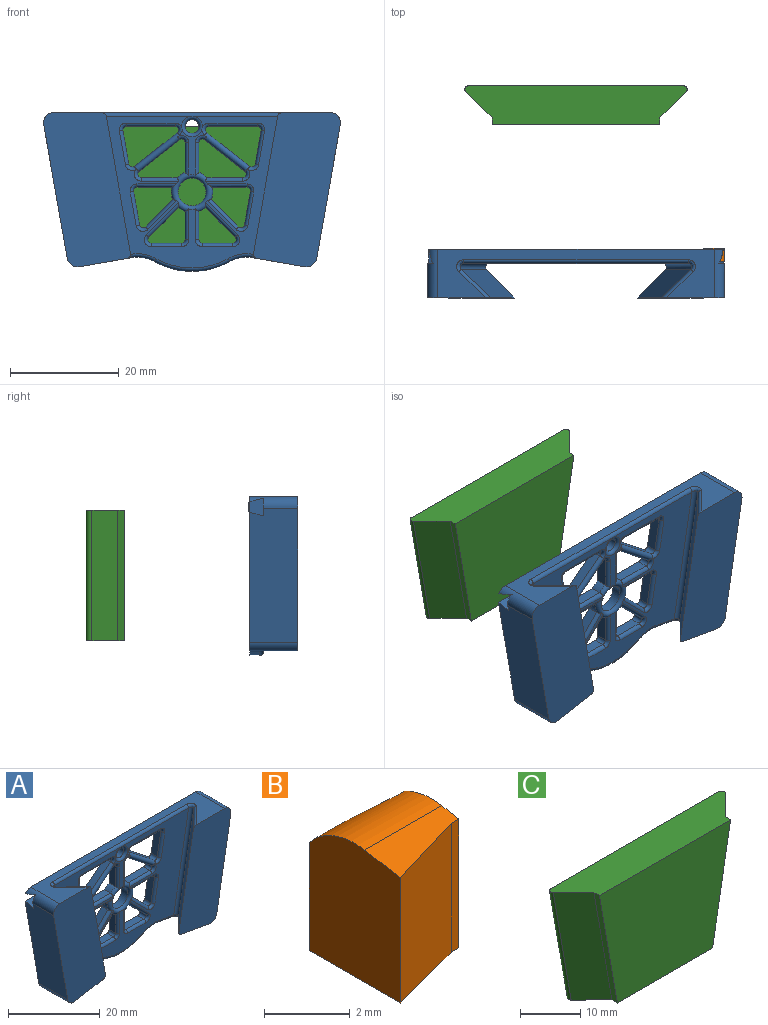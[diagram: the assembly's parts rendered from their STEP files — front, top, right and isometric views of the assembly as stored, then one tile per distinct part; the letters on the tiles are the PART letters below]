
ASSEMBLY  parts=3 mates=2
PART A: 135 faces, bbox 54.6x9.3x30.4 mm
  f0: cylinder r=1.91mm len=8.89mm, axis (0,1,0), area 25.1mm2, adj f1,f4,f5,f15,f131,f132
  f1: plane 24.58x8.89mm, normal (-0.98,0,-0.17), area 219.4mm2, adj f0,f4,f6,f15,f132,f133
  f2: plane 8.44x5.38mm, normal (0,-1,0), area 10.7mm2, adj f105,f107,f108,f112,f113,f118,f119,f124
  f3: plane 41.31x27.94mm, normal (0,-1,0), area 479.4mm2, adj f69,f70,f71,f73,f76,f77,f81,f82
  f4: plane 54.33x29.21mm, normal (0,1,0), area 1066.4mm2, adj f0,f1,f5,f6,f7,f8,f9,f10
  f5: plane 50.8x8.89mm, normal (0,0,1), area 173.2mm2, adj f0,f4,f14,f15,f16,f78,f80,f82
  f6: cylinder r=1.91mm len=8.89mm, axis (0,1,0), area 26.6mm2, adj f1,f4,f7,f15
  f7: plane 9.56x8.89mm, normal (0.17,0,-0.98), area 57.7mm2, adj f4,f6,f8,f15,f71,f72,f74
  f8: cylinder r=6.35mm len=4.21mm, axis (0,1,0), area 8.3mm2, adj f4,f7,f9,f69
  f9: cylinder r=14.2mm len=13.92mm, axis (0,1,0), area 27.7mm2, adj f4,f8,f10,f70
  f10: cylinder r=6.35mm len=4.21mm, axis (0,1,0), area 8.3mm2, adj f4,f9,f11,f73
  f11: plane 9.56x8.89mm, normal (-0.17,0,-0.98), area 57.7mm2, adj f4,f10,f12,f16,f75,f76,f79
  f12: cylinder r=1.91mm len=8.89mm, axis (0,1,0), area 26.6mm2, adj f4,f11,f13,f16
  f13: plane 24.58x8.89mm, normal (0.98,0,-0.17), area 219.4mm2, adj f4,f12,f14,f16,f127,f128
  f14: cylinder r=1.91mm len=8.89mm, axis (0,1,0), area 25.1mm2, adj f4,f5,f13,f16,f127,f129
  f15: plane 28.39x16.03mm, normal (0,-1,0), area 324.3mm2, adj f0,f1,f5,f6,f7,f17,f72,f78
  f16: plane 28.39x16.03mm, normal (0,-1,0), area 324.3mm2, adj f5,f11,f12,f13,f14,f18,f75,f84
  f17: plane 26.4x9.84mm, normal (0.7,0.71,0.12), area 196.2mm2, adj f15,f72,f77,f78
  f18: plane 26.4x9.84mm, normal (-0.7,0.71,0.12), area 196.2mm2, adj f16,f75,f81,f84
  f19: plane 5.2x1.91mm, normal (-1,0,0), area 9.9mm2, adj f4,f20,f22,f101
  f20: cylinder r=3.81mm len=1.91mm, axis (0,-1,0), area 2.7mm2, adj f4,f19,f21,f105
  f21: plane 5.47x5.47mm, normal (0.71,0,-0.71), area 14.7mm2, adj f4,f20,f23,f102
  f22: cylinder r=0.64mm len=1.91mm, axis (0,-1,0), area 1.9mm2, adj f4,f19,f24,f93
  f23: cylinder r=0.64mm len=1.91mm, axis (0,-1,0), area 2.9mm2, adj f4,f21,f24,f94
  f24: plane 5.62x1.91mm, normal (0,0,1), area 10.7mm2, adj f4,f22,f23,f87
  f25: cylinder r=1.27mm len=2.54mm, axis (0,-1,0), area 15.2mm2, adj f4,f126
  f26: cylinder r=2.54mm len=5.08mm, axis (0,-1,0), area 30.4mm2, adj f4,f105
  f27: plane 7.45x5.85mm, normal (-0.62,0,-0.79), area 18mm2, adj f4,f28,f30,f118
  f28: cylinder r=0.64mm len=1.91mm, axis (0,-1,0), area 2.7mm2, adj f4,f27,f29,f112
  f29: plane 5.55x1.91mm, normal (1,0,0), area 10.6mm2, adj f4,f28,f31,f107
  f30: cylinder r=0.64mm len=1.91mm, axis (0,-1,0), area 3mm2, adj f4,f27,f32,f111
  f31: cylinder r=3.81mm len=1.91mm, axis (0,-1,0), area 3.3mm2, adj f4,f29,f32,f105
  f32: plane 6.62x1.91mm, normal (0,0,1), area 12.6mm2, adj f4,f30,f31,f106
  f33: cylinder r=0.64mm len=1.91mm, axis (0,-1,0), area 1.9mm2, adj f4,f34,f36,f92
  f34: plane 5.62x1.91mm, normal (0,0,1), area 10.7mm2, adj f4,f33,f35,f86
  f35: cylinder r=0.64mm len=1.91mm, axis (0,-1,0), area 2.9mm2, adj f4,f34,f37,f91
  f36: plane 5.2x1.91mm, normal (1,0,0), area 9.9mm2, adj f4,f33,f38,f100
  f37: plane 5.47x5.47mm, normal (-0.71,0,-0.71), area 14.7mm2, adj f4,f35,f38,f99
  f38: cylinder r=3.81mm len=1.91mm, axis (0,-1,0), area 2.7mm2, adj f4,f36,f37,f105
  f39: plane 5.03x5.03mm, normal (0.71,0,0.71), area 13.5mm2, adj f4,f40,f42,f98
  f40: cylinder r=0.64mm len=1.91mm, axis (0,-1,0), area 2.6mm2, adj f4,f39,f41,f90
  f41: plane 6.22x1.91mm, normal (-0.98,0,0.17), area 12mm2, adj f4,f40,f43,f85
  f42: cylinder r=3.81mm len=2.27mm, axis (0,-1,0), area 4.4mm2, adj f4,f39,f44,f105
  f43: cylinder r=0.64mm len=1.91mm, axis (0,-1,0), area 2.1mm2, adj f4,f41,f44,f89
  f44: plane 6.41x1.91mm, normal (0,0,-1), area 12.2mm2, adj f4,f42,f43,f97
  f45: cylinder r=0.64mm len=1.91mm, axis (0,-1,0), area 3mm2, adj f4,f46,f48,f125
  f46: plane 8.99x1.91mm, normal (0,0,-1), area 17.1mm2, adj f4,f45,f47,f123
  f47: cylinder r=0.64mm len=1.91mm, axis (0,-1,0), area 2.1mm2, adj f4,f46,f49,f121
  f48: plane 7.9x6.21mm, normal (-0.62,0,0.79), area 19.1mm2, adj f4,f45,f50,f119
  f49: plane 6.21x1.91mm, normal (0.98,0,0.17), area 12mm2, adj f4,f47,f50,f115
  f50: cylinder r=0.64mm len=1.91mm, axis (0,-1,0), area 2.5mm2, adj f4,f48,f49,f120
  f51: plane 6.41x1.91mm, normal (0,0,-1), area 12.2mm2, adj f4,f52,f54,f104
  f52: cylinder r=0.64mm len=1.91mm, axis (0,-1,0), area 2.1mm2, adj f4,f51,f53,f96
  f53: plane 6.22x1.91mm, normal (0.98,0,0.17), area 12mm2, adj f4,f52,f55,f88
  f54: cylinder r=3.81mm len=2.27mm, axis (0,-1,0), area 4.4mm2, adj f4,f51,f56,f105
  f55: cylinder r=0.64mm len=1.91mm, axis (0,-1,0), area 2.6mm2, adj f4,f53,f56,f95
  f56: plane 5.03x5.03mm, normal (-0.71,0,0.71), area 13.5mm2, adj f4,f54,f55,f103
  f57: cylinder r=3.81mm len=1.91mm, axis (0,-1,0), area 3.3mm2, adj f4,f58,f62,f105
  f58: plane 5.55x1.91mm, normal (-1,0,0), area 10.6mm2, adj f4,f57,f59,f108
  f59: cylinder r=0.64mm len=1.91mm, axis (0,-1,0), area 2.7mm2, adj f4,f58,f60,f113
  f60: plane 7.45x5.85mm, normal (0.62,0,-0.79), area 18mm2, adj f4,f59,f61,f119
  f61: cylinder r=0.64mm len=1.91mm, axis (0,-1,0), area 3mm2, adj f4,f60,f62,f114
  f62: plane 6.62x1.91mm, normal (0,0,1), area 12.6mm2, adj f4,f57,f61,f109
  f63: plane 8.99x1.91mm, normal (0,0,-1), area 17.1mm2, adj f4,f64,f68,f122
  f64: cylinder r=0.64mm len=1.91mm, axis (0,-1,0), area 3mm2, adj f4,f63,f65,f124
  f65: plane 7.9x6.21mm, normal (0.62,0,0.79), area 19.1mm2, adj f4,f64,f66,f118
  f66: cylinder r=0.64mm len=1.91mm, axis (0,-1,0), area 2.5mm2, adj f4,f65,f67,f117
  f67: plane 6.21x1.91mm, normal (-0.98,0,0.17), area 12mm2, adj f4,f66,f68,f110
  f68: cylinder r=0.64mm len=1.91mm, axis (0,-1,0), area 2.1mm2, adj f4,f63,f67,f116
  f69: torus R=6.99mm, axis (0,-1,0), area 4.5mm2, adj f3,f8,f70,f71
  f70: torus R=13.56mm, axis (0,-1,0), area 14.3mm2, adj f3,f9,f69,f73
  f71: cylinder r=0.64mm len=4.85mm, axis (0.98,0,0.17), area 4.8mm2, adj f3,f7,f69,f74
  f72: cylinder r=0.64mm len=5.72mm, axis (0.7,-0.71,0.12), area 7.2mm2, adj f7,f15,f17,f74
  f73: torus R=6.99mm, axis (0,-1,0), area 4.5mm2, adj f3,f10,f70,f76
  f74: torus R=1.27mm, axis (0.17,0,-0.98), area 2mm2, adj f7,f71,f72,f77
  f75: cylinder r=0.64mm len=5.72mm, axis (-0.7,-0.71,0.12), area 7.2mm2, adj f11,f16,f18,f79
  f76: cylinder r=0.64mm len=4.85mm, axis (0.98,0,-0.17), area 4.8mm2, adj f3,f11,f73,f79
  f77: cylinder r=0.64mm len=26.58mm, axis (0.17,0,-0.98), area 40.1mm2, adj f3,f17,f74,f80
  f78: cylinder r=0.64mm len=5.79mm, axis (0.71,-0.7,0), area 6.7mm2, adj f5,f15,f17,f80
  f79: torus R=1.27mm, axis (0.17,0,0.98), area 2mm2, adj f11,f75,f76,f81
  f80: bspline ~2.31x1.51mm, area 1.9mm2, adj f5,f77,f78,f82
  f81: cylinder r=0.64mm len=26.58mm, axis (0.17,0,0.98), area 40.1mm2, adj f3,f18,f79,f83
  f82: cylinder r=0.64mm len=41.31mm, axis (1,0,0), area 41.2mm2, adj f3,f5,f80,f83
  f83: bspline ~2.18x1.3mm, area 1.9mm2, adj f5,f81,f82,f84
  f84: cylinder r=0.64mm len=5.79mm, axis (0.71,0.7,0), area 6.7mm2, adj f5,f16,f18,f83
  f85: cylinder r=0.64mm len=6.33mm, axis (-0.17,0,-0.98), area 6.3mm2, adj f3,f41,f89,f90
  f86: cylinder r=0.64mm len=5.62mm, axis (-1,0,0), area 5.6mm2, adj f3,f34,f91,f92
  f87: cylinder r=0.64mm len=5.62mm, axis (-1,0,0), area 5.6mm2, adj f3,f24,f93,f94
  f88: cylinder r=0.64mm len=6.33mm, axis (-0.17,0,0.98), area 6.3mm2, adj f3,f53,f95,f96
  f89: torus R=1.27mm, axis (0,-1,0), area 1.5mm2, adj f3,f43,f85,f97
  f90: torus R=1.27mm, axis (0,-1,0), area 1.9mm2, adj f3,f40,f85,f98
  f91: torus R=1.27mm, axis (0,-1,0), area 2mm2, adj f3,f35,f86,f99
  f92: torus R=1.27mm, axis (0,-1,0), area 1.4mm2, adj f3,f33,f86,f100
  f93: torus R=1.27mm, axis (0,-1,0), area 1.4mm2, adj f3,f22,f87,f101
  f94: torus R=1.27mm, axis (0,-1,0), area 2mm2, adj f3,f23,f87,f102
  f95: torus R=1.27mm, axis (0,-1,0), area 1.9mm2, adj f3,f55,f88,f103
  f96: torus R=1.27mm, axis (0,-1,0), area 1.5mm2, adj f3,f52,f88,f104
  f97: cylinder r=0.64mm len=7.32mm, axis (1,0,0), area 6.7mm2, adj f3,f44,f89,f105
  f98: cylinder r=0.64mm len=5.79mm, axis (-0.71,0,0.71), area 7.3mm2, adj f3,f39,f90,f105
  f99: cylinder r=0.64mm len=6.38mm, axis (0.71,0,-0.71), area 7.9mm2, adj f3,f37,f91,f105
  f100: cylinder r=0.64mm len=5.68mm, axis (0,0,1), area 5.4mm2, adj f3,f36,f92,f105
  f101: cylinder r=0.64mm len=5.68mm, axis (0,0,-1), area 5.4mm2, adj f3,f19,f93,f105
  f102: cylinder r=0.64mm len=6.38mm, axis (0.71,0,0.71), area 7.9mm2, adj f3,f21,f94,f105
  f103: cylinder r=0.64mm len=5.79mm, axis (-0.71,0,-0.71), area 7.3mm2, adj f3,f56,f95,f105
  f104: cylinder r=0.64mm len=7.32mm, axis (1,0,0), area 6.7mm2, adj f3,f51,f96,f105
  f105: torus R=3.17mm, axis (0,-1,0), area 29.8mm2, adj f2,f3,f20,f26,f31,f38,f42,f54
  f106: cylinder r=0.64mm len=6.9mm, axis (-1,0,0), area 6.7mm2, adj f3,f32,f105,f111
  f107: cylinder r=0.64mm len=6.03mm, axis (0,0,1), area 5.7mm2, adj f2,f29,f105,f112
  f108: cylinder r=0.64mm len=6.03mm, axis (0,0,-1), area 5.7mm2, adj f2,f58,f105,f113
  f109: cylinder r=0.64mm len=6.9mm, axis (-1,0,0), area 6.7mm2, adj f3,f62,f105,f114
  f110: cylinder r=0.64mm len=6.32mm, axis (-0.17,0,-0.98), area 6.3mm2, adj f3,f67,f116,f117
  f111: torus R=1.27mm, axis (0,-1,0), area 2.1mm2, adj f3,f30,f106,f118
  f112: torus R=1.27mm, axis (0,-1,0), area 1.9mm2, adj f2,f28,f107,f118
  f113: torus R=1.27mm, axis (0,-1,0), area 1.9mm2, adj f2,f59,f108,f119
  f114: torus R=1.27mm, axis (0,-1,0), area 2.1mm2, adj f3,f61,f109,f119
  f115: cylinder r=0.64mm len=6.32mm, axis (-0.17,0,0.98), area 6.3mm2, adj f3,f49,f120,f121
  f116: torus R=1.27mm, axis (0,-1,0), area 1.5mm2, adj f3,f68,f110,f122
  f117: torus R=1.27mm, axis (0,-1,0), area 1.8mm2, adj f3,f66,f110,f118
  f118: cylinder r=0.64mm len=8.68mm, axis (0.79,0,-0.62), area 19.5mm2, adj f2,f3,f27,f65,f111,f112,f117,f124
  f119: cylinder r=0.64mm len=8.68mm, axis (0.79,0,0.62), area 19.5mm2, adj f2,f3,f48,f60,f113,f114,f120,f125
  f120: torus R=1.27mm, axis (0,-1,0), area 1.8mm2, adj f3,f50,f115,f119
  f121: torus R=1.27mm, axis (0,-1,0), area 1.5mm2, adj f3,f47,f115,f123
  f122: cylinder r=0.64mm len=8.99mm, axis (1,0,0), area 9mm2, adj f3,f63,f116,f124
  f123: cylinder r=0.64mm len=8.99mm, axis (1,0,0), area 9mm2, adj f3,f46,f121,f125
  f124: torus R=1.27mm, axis (0,-1,0), area 2.1mm2, adj f2,f3,f64,f118,f122,f126
  f125: torus R=1.27mm, axis (0,-1,0), area 2.1mm2, adj f2,f3,f45,f119,f123,f126
  f126: torus R=1.91mm, axis (0,-1,0), area 9.4mm2, adj f2,f3,f25,f124,f125
  f127: plane 3.81x3.27mm, normal (0,1,0), area 11.8mm2, adj f13,f14,f128,f129,f130
  f128: plane 3.67x2.54mm, normal (0,-0.26,0.97), area 9.5mm2, adj f4,f13,f127,f130
  f129: plane 3.55x2.54mm, normal (0,-0.26,-0.97), area 8.6mm2, adj f4,f14,f127,f130
  f130: plane 3.27x2.54mm, normal (1,0,0), area 6.6mm2, adj f4,f127,f128,f129
  f131: plane 3.55x2.54mm, normal (0,-0.26,-0.97), area 8.6mm2, adj f0,f4,f132,f134
  f132: plane 3.81x3.27mm, normal (0,1,0), area 11.8mm2, adj f0,f1,f131,f133,f134
  f133: plane 3.67x2.54mm, normal (0,-0.26,0.97), area 9.5mm2, adj f1,f4,f132,f134
  f134: plane 3.27x2.54mm, normal (-1,0,0), area 6.6mm2, adj f4,f131,f132,f133
PART B: 9 faces, bbox 2.5x3x3.8 mm
  f0: plane 3x2.54mm, normal (0,0,-1), area 5.9mm2, adj f1,f2,f5,f6,f7,f8
  f1: plane 3.59x2.29mm, normal (0.26,0.97,0), area 8mm2, adj f0,f3,f5,f8
  f2: plane 3.68x2.29mm, normal (0.26,-0.97,0), area 8.6mm2, adj f0,f4,f6,f8
  f3: cylinder r=1.91mm len=2.54mm, axis (1,0,0), area 4.1mm2, adj f1,f4,f5,f7,f8
  f4: plane 2.54x1.17mm, normal (0,-0.17,0.98), area 2.2mm2, adj f2,f3,f6,f7,f8
  f5: plane 3.59x0.25mm, normal (0,1,0), area 0.9mm2, adj f0,f1,f3,f7
  f6: plane 3.68x0.25mm, normal (0,-1,0), area 0.9mm2, adj f0,f2,f4,f7
  f7: plane 3.81x1.78mm, normal (1,0,0), area 6.7mm2, adj f0,f3,f4,f5,f6
  f8: plane 3.81x3mm, normal (-1,0,0), area 11mm2, adj f0,f1,f2,f3,f4
PART C: 10 faces, bbox 40.9x7.1x24.2 mm
  f0: plane 39.64x24mm, normal (0,1,0), area 849.7mm2, adj f1,f4,f8,f9
  f1: plane 32.46x7.11mm, normal (0,0,-1), area 193.1mm2, adj f0,f2,f3,f5,f6,f7,f8,f9
  f2: plane 24x9.06mm, normal (-0.7,-0.71,-0.12), area 164mm2, adj f1,f4,f6,f9
  f3: plane 24x9.06mm, normal (0.7,-0.71,-0.12), area 164mm2, adj f1,f4,f5,f8
  f4: plane 40.92x7.11mm, normal (0,0,1), area 253.3mm2, adj f0,f2,f3,f5,f6,f7,f8,f9
  f5: plane 24x4.23mm, normal (0.98,0,-0.17), area 30.9mm2, adj f1,f3,f4,f7
  f6: plane 24x4.23mm, normal (-0.98,0,-0.17), area 30.9mm2, adj f1,f2,f4,f7
  f7: plane 30.88x24mm, normal (0,-1,0), area 639.7mm2, adj f1,f4,f5,f6
  f8: cylinder r=0.64mm len=24.22mm, axis (-0.17,0,-0.98), area 36.5mm2, adj f0,f1,f3,f4
  f9: cylinder r=0.64mm len=24.22mm, axis (-0.17,0,0.98), area 36.5mm2, adj f0,f1,f2,f4
PLACE A t=(-1.42,4.61,1.47)mm fixed
PLACE B rot(axis=(0.58,0.58,0.58),120deg) t=(22.08,2.07,14.2)mm
PLACE C t=(-1.42,34.68,3.42)mm
MATE slider C.f0 <-> A.f25  axis (0,1,0) through (-1.42,34.68,13.53)mm
MATE planar A.f130 <-> B.f0  axis (1,0,0) through (22.08,3.22,14.17)mm
